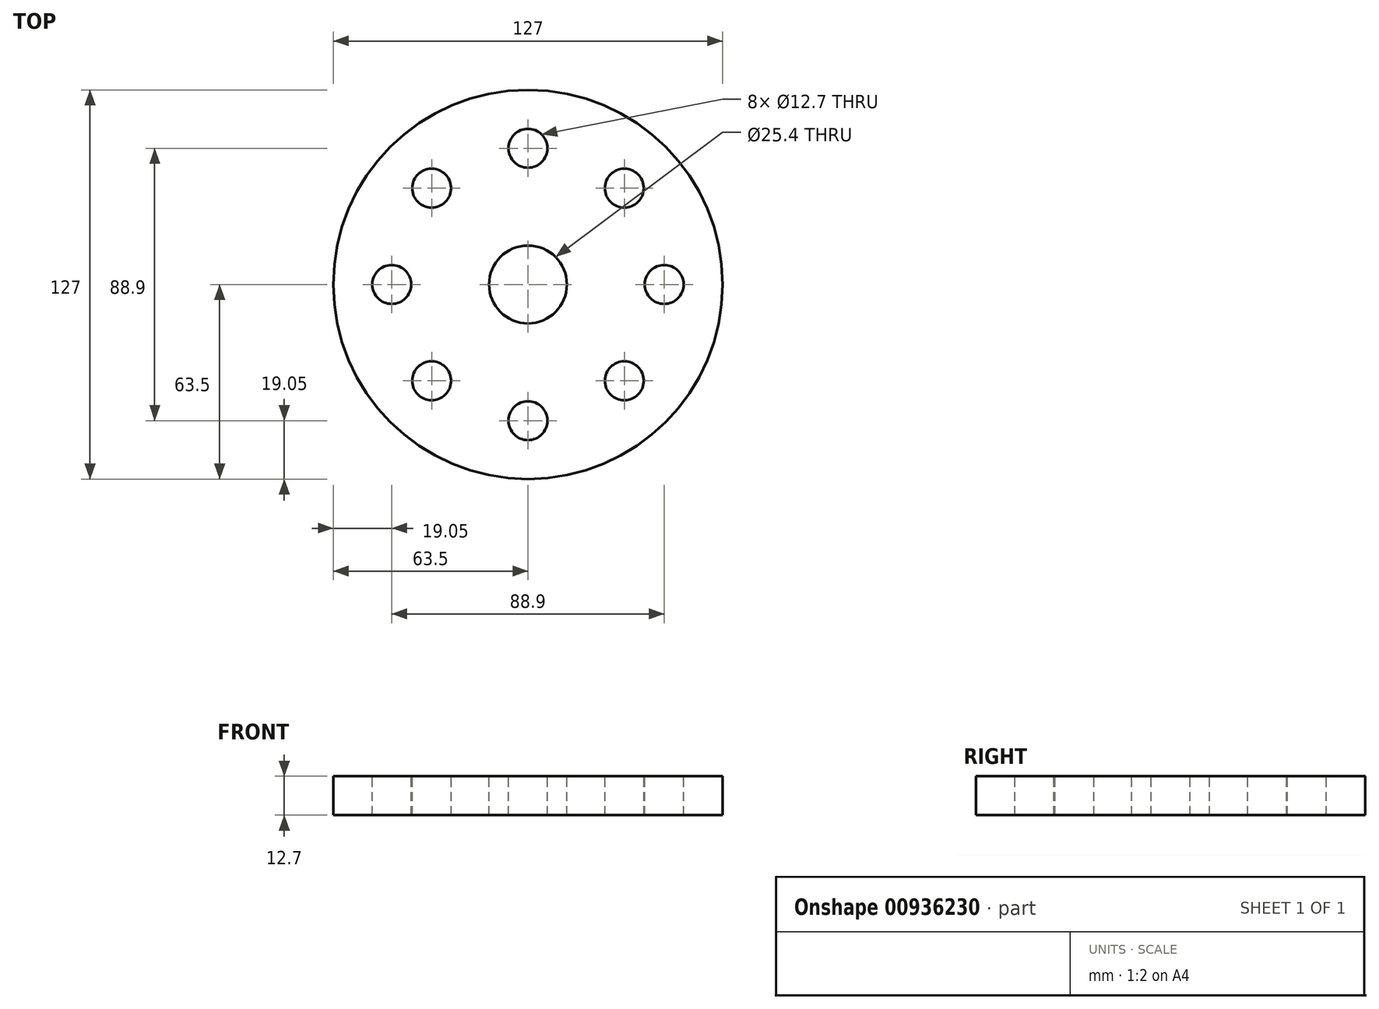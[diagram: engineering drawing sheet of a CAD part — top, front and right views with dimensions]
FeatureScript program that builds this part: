
annotation { "Feature Type Name" : "Feature", "Feature Type Description" : "" }
export const myFeature = defineFeature(function(context is Context, id is Id, definition is map)
    precondition{}
    {
        {
            var Q0;
            Q0=qCreatedBy(makeId("Top.planeOp"),FACE);
            var sketch = newSketch(context, id + "F0", { "sketchPlane" : qUnion([Q0])});
            skCircle(sketch, "E0", {"center": v(0, 0) * mm, "radius": 63.5 * mm});
            skCircle(sketch, "E1", {"center": v(0, 44.45) * mm, "radius": 6.35 * mm});
            skCircle(sketch, "E2.1.0", {"center": v(-31.43, 31.43) * mm, "radius": 6.35 * mm});
            skCircle(sketch, "E2.2.0", {"center": v(-44.45, 0) * mm, "radius": 6.35 * mm});
            skCircle(sketch, "E2.3.0", {"center": v(-31.43, -31.43) * mm, "radius": 6.35 * mm});
            skCircle(sketch, "E2.4.0", {"center": v(0, -44.45) * mm, "radius": 6.35 * mm});
            skCircle(sketch, "E2.5.0", {"center": v(31.43, -31.43) * mm, "radius": 6.35 * mm});
            skCircle(sketch, "E2.6.0", {"center": v(44.45, 0) * mm, "radius": 6.35 * mm});
            skCircle(sketch, "E2.7.0", {"center": v(31.43, 31.43) * mm, "radius": 6.35 * mm});
            skCircle(sketch, "E3", {"center": v(0, 0) * mm, "radius": 12.7 * mm});
            skSolve(sketch);
        }
        {
            var Q0;
            Q0=makeQuery(id+"F0.imprint","IMPRINT",FACE,{"disambiguationData":[TD([[makeQuery(id+"F0.imprint","IMPRINT",EDGE,{"derivedFrom":sQuery(id+"F0.wireOp",EDGE,"E0")}),1.0]])]});
            extrude(context, id + "F1", {"entities" : qUnion([Q0]), "oppositeDirection" : true, "depth" : 12.7 * mm, "offsetDistance" : 25.4 * mm});
        }
    });
